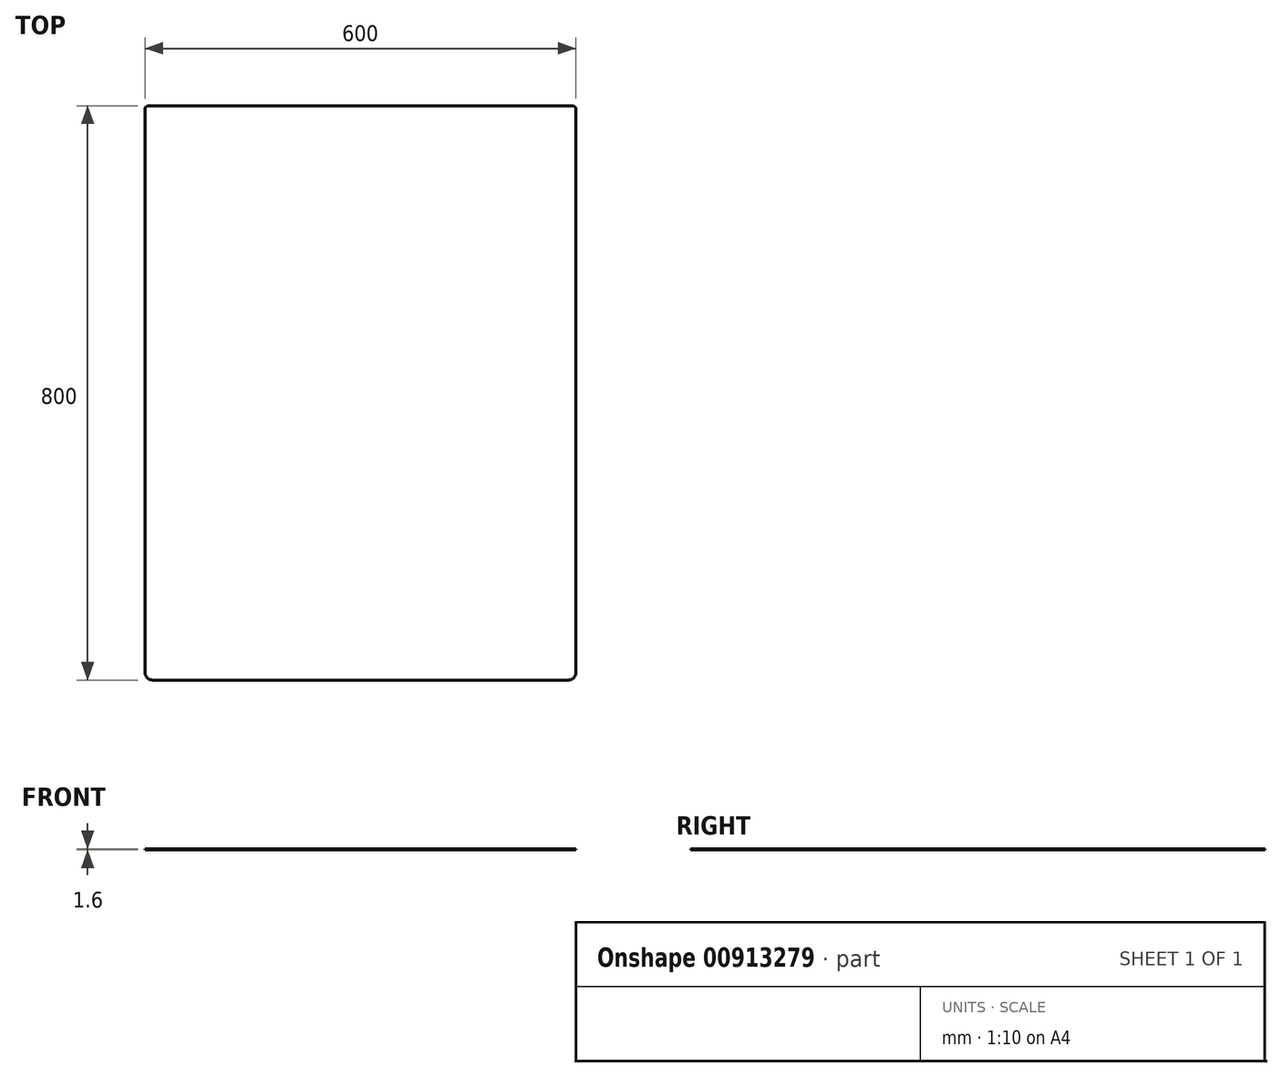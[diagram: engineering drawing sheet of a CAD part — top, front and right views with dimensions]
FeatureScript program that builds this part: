
annotation { "Feature Type Name" : "Feature", "Feature Type Description" : "" }
export const myFeature = defineFeature(function(context is Context, id is Id, definition is map)
    precondition{}
    {
        {
            var Q0;
            Q0=qCreatedBy(makeId("Top.planeOp"),FACE);
            var sketch = newSketch(context, id + "F0", { "sketchPlane" : qUnion([Q0])});
            skLineSegment(sketch, "E0.bottom", {"start": v(-453.86, 765.3) * mm, "end": v(146.14, 765.3) * mm});
            skLineSegment(sketch, "E0.top", {"start": v(-453.86, -34.7) * mm, "end": v(146.14, -34.7) * mm});
            skLineSegment(sketch, "E0.left", {"start": v(-453.86, 765.3) * mm, "end": v(-453.86, -34.7) * mm});
            skLineSegment(sketch, "E0.right", {"start": v(146.14, 765.3) * mm, "end": v(146.14, -34.7) * mm});
            skSolve(sketch);
        }
        {
            var Q0;
            Q0 = qSketchRegion(id + "F0", true);
            extrude(context, id + "F1", {"entities" : qUnion([Q0]), "depth" : 1.6 * mm, "offsetDistance" : 25 * mm});
        }
        {
            var Q0;
            Q0=makeQuery(id+"F1.opExtrude","SWEPT_EDGE",EDGE,{"disambiguationData":[OSD([sQuery(id+"F0.wireOp",EDGE,"E0.top"),sQuery(id+"F0.wireOp",EDGE,"E0.right")])]});
            fillet(context, id + "F2", {"entities" : qUnion([Q0]), "radius" : 10 * mm, "tangentPropagation" : true, "allowEdgeOverflow" : false});
        }
        {
            var Q0;
            Q0=makeQuery(id+"F1.opExtrude","SWEPT_EDGE",EDGE,{"disambiguationData":[OSD([sQuery(id+"F0.wireOp",EDGE,"E0.top"),sQuery(id+"F0.wireOp",EDGE,"E0.left")])]});
            fillet(context, id + "F3", {"entities" : qUnion([Q0]), "radius" : 10 * mm, "tangentPropagation" : true, "allowEdgeOverflow" : false});
        }
        {
            var Q0;
            Q0=makeQuery(id+"F1.opExtrude","SWEPT_EDGE",EDGE,{"disambiguationData":[OSD([sQuery(id+"F0.wireOp",EDGE,"E0.bottom"),sQuery(id+"F0.wireOp",EDGE,"E0.right")])]});
            chamfer(context, id + "F4", {"entities" : qUnion([Q0]), "width" : 3 * mm, "tangentPropagation" : true});
        }
        {
            var Q0;
            Q0=makeQuery(id+"F1.opExtrude","SWEPT_EDGE",EDGE,{"disambiguationData":[OSD([sQuery(id+"F0.wireOp",EDGE,"E0.bottom"),sQuery(id+"F0.wireOp",EDGE,"E0.left")])]});
            chamfer(context, id + "F5", {"entities" : qUnion([Q0]), "width" : 3 * mm, "tangentPropagation" : true});
        }
    });
